# Revit family: Cleverfit Pro LED Exit_R16
name_source: partatom
category: Lighting Fixtures
revit_build: Autodesk Revit LT 2016 (Build: 20150220_1215(x64)
units: mm (PartAtom-declared; Revit-internal decimal feet)

## family parameters
Cut with Voids When Loaded = No
Host = Face
Light Source = Yes
Part Type = Normal
Room Calculation Point = No
Round Connector Dimension = Use Diameter
Shared = No

## types (5) — shared parameters
AS2293 = C0=D4 C90=E8 C180=D4 C270=E8
Apparent Load = 4 VA
Ballast = Electronic
Color Filter = 16777215
Construction = Fire-retardant PC/ABS body with Polycarbonate Diffusers
Default Elevation = 1219 mm
Diffuser = All directional inserts included in the box
Dimming Lamp Color Temperature Shift = <None>
Emit Shape Visible in Rendering = No
Emit from Circle Diameter = 610 mm
Family Type = Sign
Height = 214 mm  [stored 0.7021 ft]
IP Rating = IP20
Lamp = 2 x 1W LED 100,000 hours
Length = 367 mm  [stored 1.20407 ft]
Manufacturer = Clevertronics
Mounting = Surface Mount. Single Side Wall. Single or Double Side Ceiling.
Operating Mode = Maintained
Operating Temperature = 0°C to +40°C
Operating Voltage = 240 V
Photometric Web File = ll15872 LCFPRO-ZW.IES
Power Consumption = 4 W
Sign Height = 3 mm  [stored 0.00984252 ft]
Sign Length = 353 mm  [stored 1.15814 ft]
Sign Width = 178 mm  [stored 0.58399 ft]
Tilt Angle = -90.00°
Viewing Distance = 24000 mm  [stored 78.7402 ft]
Wattage Comments = Standby
Width = 72 mm  [stored 0.23622 ft]

## per-type parameters (varying)
| type | Charging Method | Description | Testing System |
| LCFPRO-CT | Intelligent current limited constant voltage charger | LED Cleverfit Pro Exit | Clever-Test |
| LCFPRO | Intelligent current limited constant voltage charger | LED Cleverfit Pro Exit | N/A - Manual Test Switch |
| LCFPRO-DALI | Intelligent current limited constant voltage charger | LED Cleverfit Pro Exit with DALI | DALI Compatible |
| LCFPRO-DATA | Intelligent current limited constant voltage charger | LED Cleverfit Pro Exit | Zoneworks DATA Computerized Testing |
| LCFPRO-ZW | Constant current to 3.4V, then constant voltage | LED Cleverfit Pro Exit | Zoneworks Computerized Testing |

note: column(s) folded — value = type name in every type: Model

note: [stored X ft] marks values corroborated as IEEE doubles in the binary element streams (Revit-internal decimal feet)

## geometry (parser evidence)
native form markers: Sweep x3
no freeform markers — native parametric forms only
